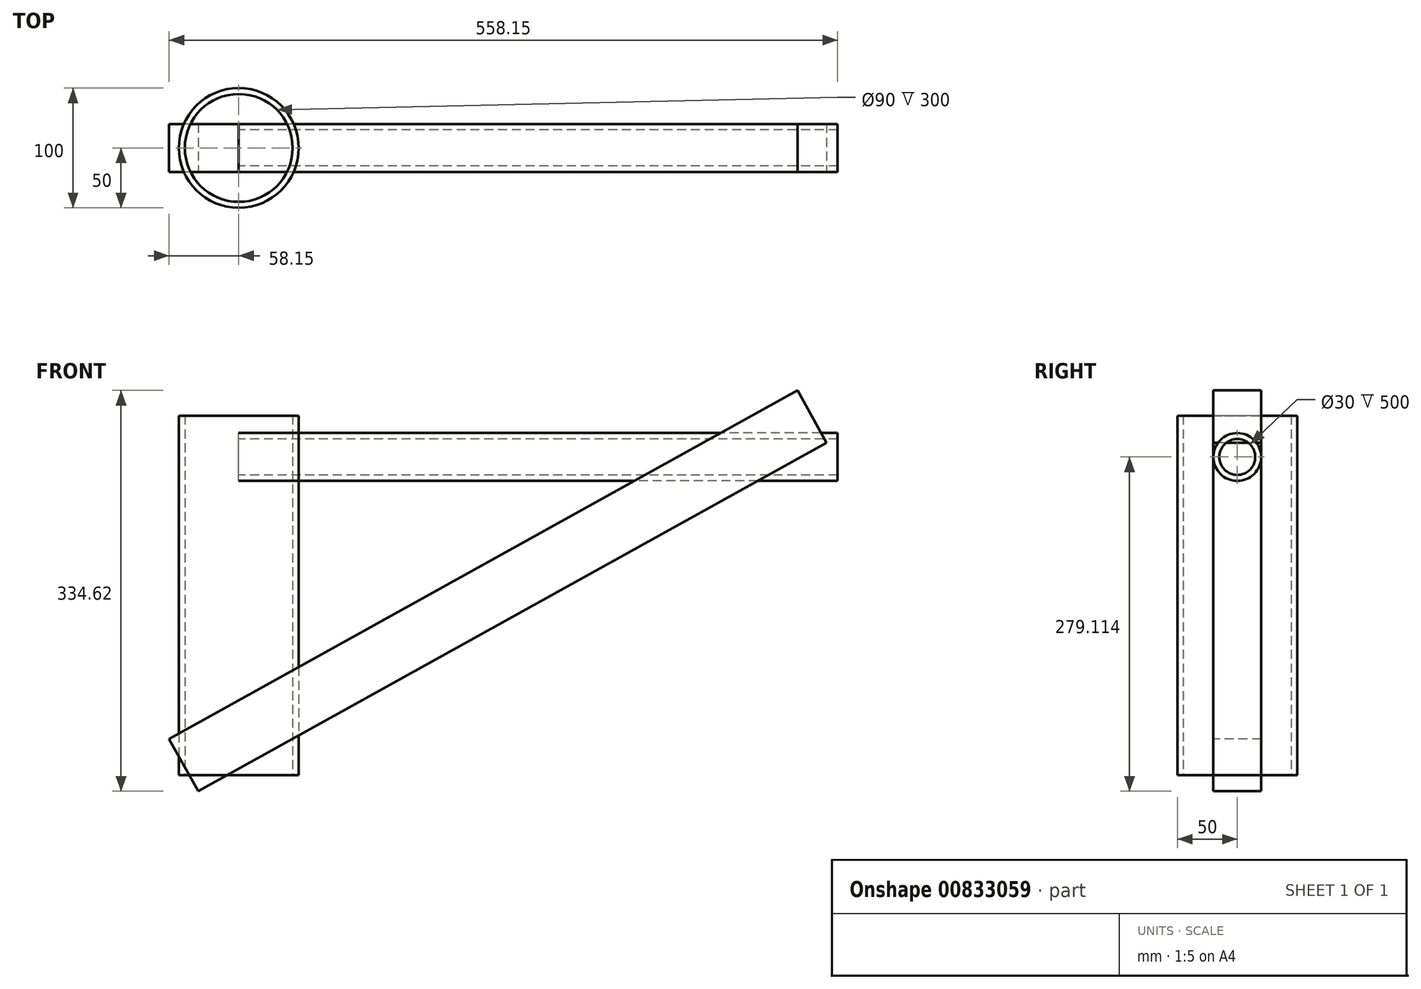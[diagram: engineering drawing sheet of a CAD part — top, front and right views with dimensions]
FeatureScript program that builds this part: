
annotation { "Feature Type Name" : "Feature", "Feature Type Description" : "" }
export const myFeature = defineFeature(function(context is Context, id is Id, definition is map)
    precondition{}
    {
        {
            var Q0;
            Q0=qCreatedBy(makeId("Top.planeOp"),FACE);
            var sketch = newSketch(context, id + "F0", { "sketchPlane" : qUnion([Q0])});
            skCircle(sketch, "E0", {"center": v(0, 0) * mm, "radius": 50 * mm});
            skCircle(sketch, "E1", {"center": v(0, 0) * mm, "radius": 45 * mm});
            skSolve(sketch);
        }
        {
            var Q0;
            Q0=makeQuery(id+"F0.imprint","IMPRINT",FACE,{"disambiguationData":[TD([[makeQuery(id+"F0.imprint","IMPRINT",EDGE,{"derivedFrom":sQuery(id+"F0.wireOp",EDGE,"E0")}),1.0]])]});
            extrude(context, id + "F1", {"entities" : qUnion([Q0]), "depth" : 300 * mm, "offsetDistance" : 25 * mm});
        }
        {
            var Q0;
            Q0=qCreatedBy(makeId("Top.planeOp"),FACE);
            cPlane(context, id + "F2", {"entities" : qUnion([Q0]), "cplaneType" : CPlaneType.OFFSET, "offset" : 25 * mm, "width" : 150 * mm, "height" : 150 * mm});
        }
        {
            var Q0;
            Q0=qCreatedBy(id+"F2.planeOp",FACE);
            var sketch = newSketch(context, id + "F3", { "sketchPlane" : qUnion([Q0])});
            skLineSegment(sketch, "E2", {"start": v(-55.3, 45.58) * mm, "end": v(-55.3, -50.98) * mm});
            skSolve(sketch);
        }
        {
            var Q0;
            Q0=qCreatedBy(id+"F2.planeOp",FACE);
            var Q1;
            Q1=sQuery(id+"F3.wireOp",EDGE,"E2");
            cPlane(context, id + "F4", {"entities" : qUnion([Q0, Q1]), "cplaneType" : CPlaneType.LINE_ANGLE, "offset" : 25 * mm, "angle" : 61 * degree, "oppositeDirection" : true, "width" : 150 * mm, "height" : 150 * mm});
        }
        {
            var Q0;
            Q0=qCreatedBy(id+"F4.planeOp",FACE);
            var sketch = newSketch(context, id + "F5", { "sketchPlane" : qUnion([Q0])});
            skLineSegment(sketch, "E3.bottom", {"start": v(-20, 4.55) * mm, "end": v(20, 4.55) * mm});
            skLineSegment(sketch, "E3.top", {"start": v(-20, 54.55) * mm, "end": v(20, 54.55) * mm});
            skLineSegment(sketch, "E3.left", {"start": v(-20, 4.55) * mm, "end": v(-20, 54.55) * mm});
            skLineSegment(sketch, "E3.right", {"start": v(20, 4.55) * mm, "end": v(20, 54.55) * mm});
            skSolve(sketch);
        }
        {
            var Q0;
            Q0=makeQuery(id+"F5.imprint","IMPRINT",FACE,{"disambiguationData":[TD([[makeQuery(id+"F5.imprint","IMPRINT",EDGE,{"derivedFrom":sQuery(id+"F5.wireOp",EDGE,"E3.bottom")}),1.0]])]});
            extrude(context, id + "F6", {"entities" : qUnion([Q0]), "oppositeDirection" : true, "depth" : 600 * mm, "offsetDistance" : 25 * mm});
        }
        {
            var Q0;
            Q0=qCreatedBy(makeId("Right.planeOp"),FACE);
            var sketch = newSketch(context, id + "F7", { "sketchPlane" : qUnion([Q0])});
            skCircle(sketch, "E4", {"center": v(0, 265.52) * mm, "radius": 20 * mm});
            skCircle(sketch, "E5", {"center": v(0, 265.52) * mm, "radius": 15 * mm});
            skSolve(sketch);
        }
        {
            var Q0;
            Q0=makeQuery(id+"F7.imprint","IMPRINT",FACE,{"disambiguationData":[TD([[makeQuery(id+"F7.imprint","IMPRINT",EDGE,{"derivedFrom":sQuery(id+"F7.wireOp",EDGE,"E4")}),1.0]])]});
            extrude(context, id + "F8", {"entities" : qUnion([Q0]), "depth" : 500 * mm, "offsetDistance" : 25 * mm});
        }
    });
